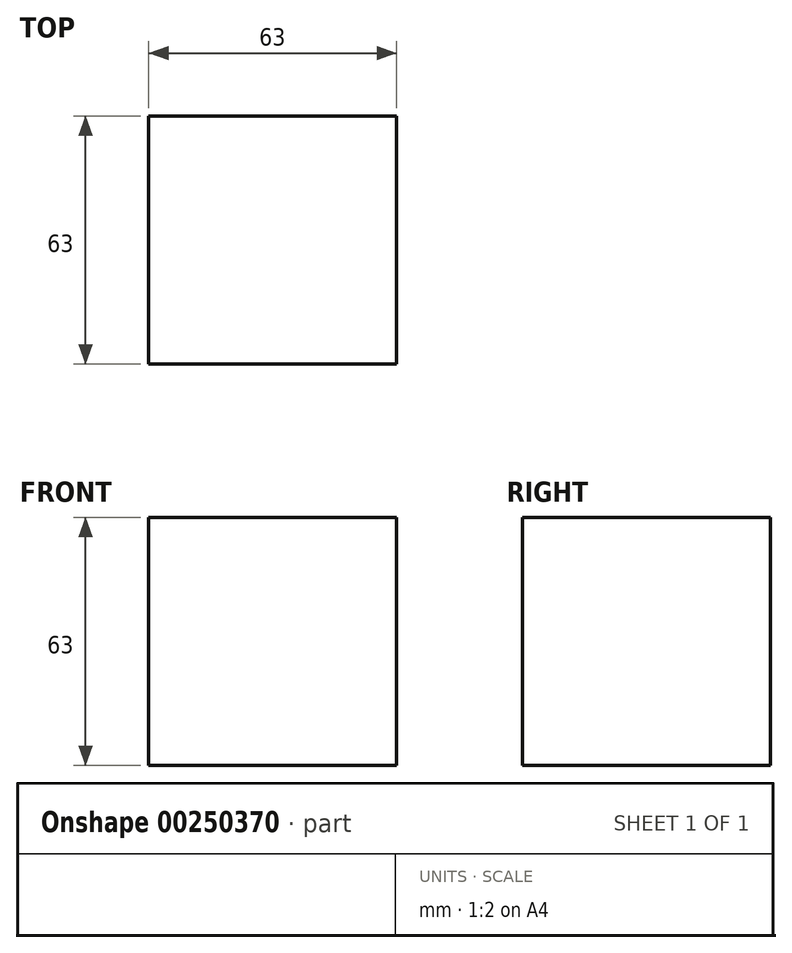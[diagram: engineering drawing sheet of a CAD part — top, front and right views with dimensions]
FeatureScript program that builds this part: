
annotation { "Feature Type Name" : "Feature", "Feature Type Description" : "" }
export const myFeature = defineFeature(function(context is Context, id is Id, definition is map)
    precondition{}
    {
        {
            var Q0;
            Q0=qCreatedBy(makeId("Front.planeOp"),FACE);
            var sketch = newSketch(context, id + "F0", { "sketchPlane" : qUnion([Q0])});
            skLineSegment(sketch, "E0.bottom", {"start": v(31.5, -31.5) * mm, "end": v(-31.5, -31.5) * mm});
            skLineSegment(sketch, "E0.top", {"start": v(31.5, 31.5) * mm, "end": v(-31.5, 31.5) * mm});
            skLineSegment(sketch, "E0.left", {"start": v(31.5, -31.5) * mm, "end": v(31.5, 31.5) * mm});
            skLineSegment(sketch, "E0.right", {"start": v(-31.5, -31.5) * mm, "end": v(-31.5, 31.5) * mm});
            skPoint(sketch, "E0.middle", {"position": v(0, 0) * mm});
            skSolve(sketch);
        }
        {
            var Q0;
            Q0 = qSketchRegion(id + "F0", true);
            extrude(context, id + "F1", {"entities" : qUnion([Q0]), "depth" : 63 * mm});
        }
    });
